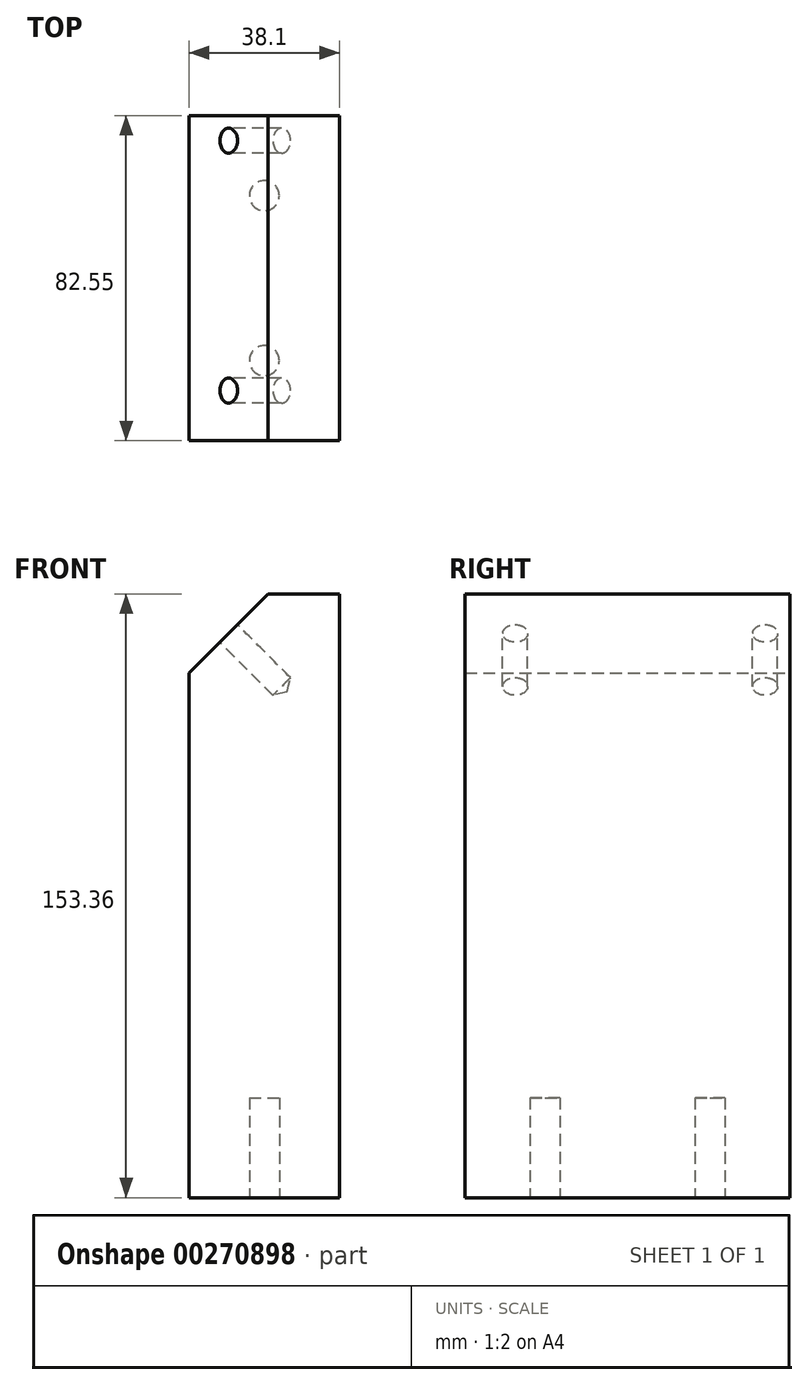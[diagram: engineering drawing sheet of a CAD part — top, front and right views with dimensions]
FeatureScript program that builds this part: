
annotation { "Feature Type Name" : "Feature", "Feature Type Description" : "" }
export const myFeature = defineFeature(function(context is Context, id is Id, definition is map)
    precondition{}
    {
        {
            var Q0;
            Q0=qCreatedBy(makeId("Front.planeOp"),FACE);
            var sketch = newSketch(context, id + "F0", { "sketchPlane" : qUnion([Q0])});
            skLineSegment(sketch, "E0.bottom", {"start": v(0, -12.32) * mm, "end": v(38.1, -12.32) * mm});
            skLineSegment(sketch, "E0.top", {"start": v(20.02, 141.04) * mm, "end": v(38.1, 141.04) * mm});
            skLineSegment(sketch, "E0.left", {"start": v(0, -12.32) * mm, "end": v(0, 121.03) * mm});
            skLineSegment(sketch, "E0.right", {"start": v(38.1, -12.32) * mm, "end": v(38.1, 141.04) * mm});
            skLineSegment(sketch, "E1", {"start": v(0, 121.03) * mm, "end": v(20.02, 141.04) * mm});
            skSolve(sketch);
        }
        {
            var Q0;
            Q0 = qSketchRegion(id + "F0", true);
            extrude(context, id + "F1", {"entities" : qUnion([Q0]), "depth" : 82.55 * mm});
        }
        {
            var Q0;
            Q0=makeQuery(id+"F1.opExtrude","SWEPT_FACE",FACE,{"disambiguationData":[OSD([sQuery(id+"F0.wireOp",EDGE,"E0.bottom")])]});
            var sketch = newSketch(context, id + "F2", { "sketchPlane" : qUnion([Q0])});
            skCircle(sketch, "E2", {"center": v(19.05, 62.23) * mm, "radius": 3.81 * mm});
            skPoint(sketch, "E2.centerSnap0", {"position": v(19.05, 82.55) * mm});
            skCircle(sketch, "E3", {"center": v(19.05, 20.32) * mm, "radius": 3.81 * mm});
            skSolve(sketch);
        }
        {
            var Q0;
            Q0 = qSketchRegion(id + "F2", true);
            extrude(context, id + "F3", {"entities" : qUnion([Q0]), "operationType" : NewBodyOperationType.REMOVE, "oppositeDirection" : true, "depth" : 25.4 * mm});
        }
        {
            var Q0;
            Q0=makeQuery(id+"F1.opExtrude","SWEPT_FACE",FACE,{"disambiguationData":[OSD([sQuery(id+"F0.wireOp",EDGE,"E1")])]});
            var sketch = newSketch(context, id + "F4", { "sketchPlane" : qUnion([Q0])});
            skPoint(sketch, "E4", {"position": v(0, 99.73) * mm});
            skPoint(sketch, "E5", {"position": v(6.35, 99.73) * mm});
            skPoint(sketch, "E6", {"position": v(69.85, 99.73) * mm});
            skSolve(sketch);
        }
        {
            var Q0;
            Q0=sQuery(id+"F4.wireOp",VERTEX,"E5");
            var Q1;
            Q1=sQuery(id+"F4.wireOp",VERTEX,"E6");
            var Q2;
            Q2=makeQuery(id+"F1.opExtrude","SWEPT_BODY",BODY,{"disambiguationData":[OSD([sQuery(id+"F0.wireOp",EDGE,"E0.bottom"),sQuery(id+"F0.wireOp",EDGE,"E0.top"),sQuery(id+"F0.wireOp",EDGE,"E0.left"),sQuery(id+"F0.wireOp",EDGE,"E0.right"),sQuery(id+"F0.wireOp",EDGE,"E1")])]});
            hole(context, id + "F5", {"style" : HoleStyle.SIMPLE, "endStyle" : HoleEndStyle.BLIND, "holeDiameter" : 6.35 * mm, "holeDepth" : 19.05 * mm, "tappedDepth" : 12.7 * mm, "tapClearance" : 3, "locations" : qUnion([Q0, Q1]), "scope" : qUnion([Q2])});
        }
    });
